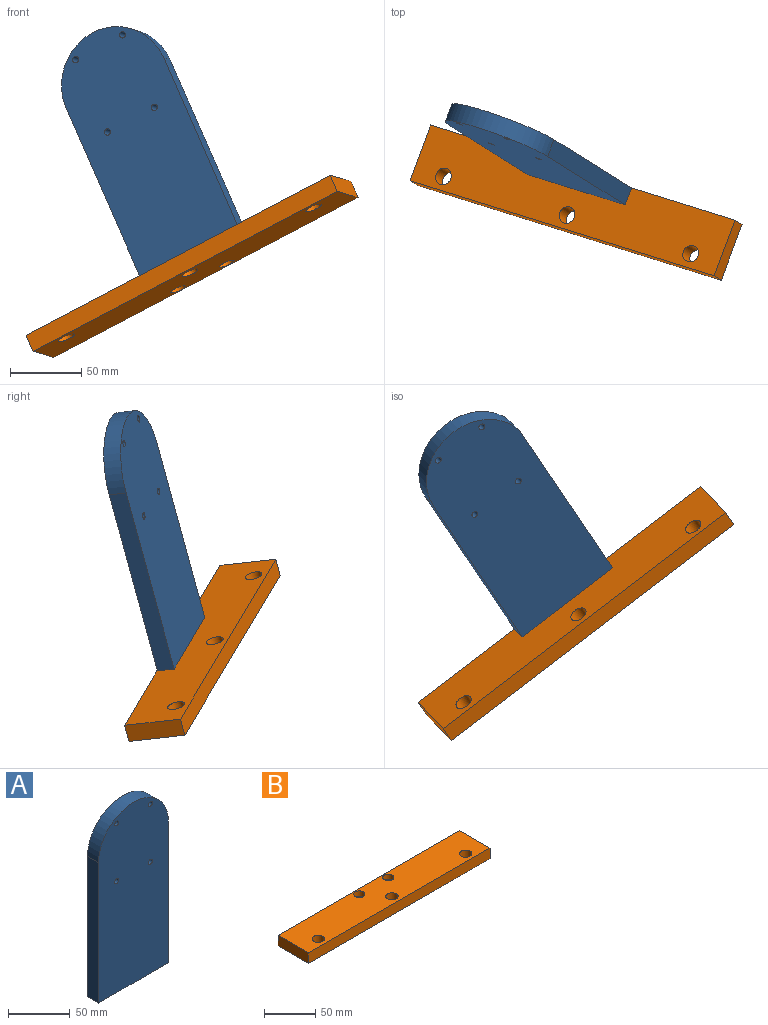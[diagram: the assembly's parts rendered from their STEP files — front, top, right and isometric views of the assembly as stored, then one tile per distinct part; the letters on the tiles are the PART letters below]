
ASSEMBLY  parts=2 mates=1
PART A: 14 faces, bbox 80x12.7x179 mm
  f0: cylinder r=40mm len=80mm, axis (0,1,0), area 1595.9mm2, adj f1,f3,f4,f5
  f1: plane 139x12.7mm, normal (-1,0,0), area 1765.3mm2, adj f0,f2,f4,f5
  f2: plane 80x12.7mm, normal (0,0,-1), area 947.6mm2, adj f1,f3,f4,f5,f11,f13
  f3: plane 139x12.7mm, normal (1,0,0), area 1765.3mm2, adj f0,f2,f4,f5
  f4: plane 179x80mm, normal (0,-1,0), area 13569.7mm2, adj f0,f1,f2,f3,f6,f7,f8,f9
  f5: plane 179x80mm, normal (0,1,0), area 13569.7mm2, adj f0,f1,f2,f3,f6,f7,f8,f9
  f6: cylinder r=2.25mm len=12.7mm, axis (0,1,0), area 179.5mm2, adj f4,f5
  f7: cylinder r=2.25mm len=12.7mm, axis (0,1,0), area 179.5mm2, adj f4,f5
  f8: cylinder r=2.25mm len=12.7mm, axis (0,1,0), area 179.5mm2, adj f4,f5
  f9: cylinder r=2.25mm len=12.7mm, axis (0,1,0), area 179.5mm2, adj f4,f5
  f10: cone r=0mm half-angle=59deg, axis (0,0,-1), area 39.9mm2, adj f11
  f11: cylinder r=3.3mm len=12.65mm, axis (0,0,-1), area 262.3mm2, adj f2,f10
  f12: cone r=0mm half-angle=59deg, axis (0,0,-1), area 39.9mm2, adj f13
  f13: cylinder r=3.3mm len=12.65mm, axis (0,0,-1), area 262.3mm2, adj f2,f12
PART B: 15 faces, bbox 250x42x12.7 mm
  f0: plane 42x12.7mm, normal (-1,0,0), area 533.4mm2, adj f1,f3,f4,f5
  f1: plane 250x12.7mm, normal (0,-1,0), area 3175mm2, adj f0,f2,f4,f5
  f2: plane 42x12.7mm, normal (1,0,0), area 533.4mm2, adj f1,f3,f4,f5
  f3: plane 250x12.7mm, normal (0,1,0), area 3175mm2, adj f0,f2,f4,f5
  f4: plane 250x42mm, normal (0,0,1), area 9970.6mm2, adj f0,f1,f2,f3,f8,f11,f12,f13
  f5: plane 250x42mm, normal (0,0,-1), area 10092.3mm2, adj f0,f1,f2,f3,f6,f9,f12,f13
  f6: cylinder r=3.3mm len=6.6mm, axis (0,0,1), area 130.6mm2, adj f5,f7
  f7: plane 11x11mm, normal (0,0,1), area 60.8mm2, adj f6,f8
  f8: cylinder r=5.5mm len=11mm, axis (0,0,1), area 221.2mm2, adj f4,f7
  f9: cylinder r=3.3mm len=6.6mm, axis (0,0,1), area 130.6mm2, adj f5,f10
  f10: plane 11x11mm, normal (0,0,1), area 60.8mm2, adj f9,f11
  f11: cylinder r=5.5mm len=11mm, axis (0,0,1), area 221.2mm2, adj f4,f10
  f12: cylinder r=6mm len=12.7mm, axis (0,0,1), area 478.8mm2, adj f4,f5
  f13: cylinder r=6mm len=12.7mm, axis (0,0,1), area 478.8mm2, adj f4,f5
  f14: cylinder r=6mm len=12.7mm, axis (0,0,1), area 478.8mm2, adj f4,f5
PLACE A rot(axis=(-0.22,0.09,0.97),161.6deg) t=(349.03,698.08,1200.36)mm
PLACE B rot(axis=(0.16,0.98,-0.09),154.7deg) t=(499.86,603.79,1135.97)mm
MATE parallel B.f6 <-> A.f10  axis (-0.39,0.24,0.89) through (388.31,675.19,1067.35)mm
